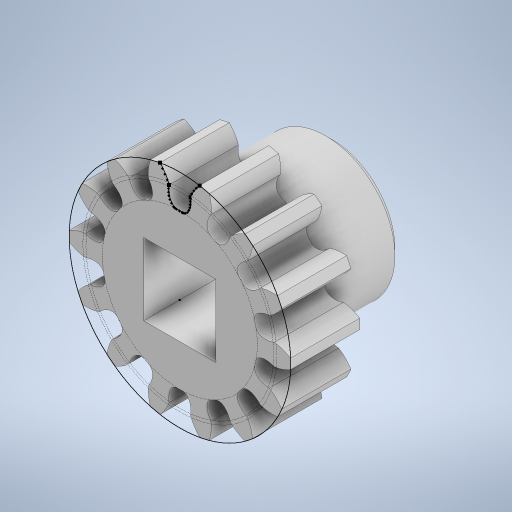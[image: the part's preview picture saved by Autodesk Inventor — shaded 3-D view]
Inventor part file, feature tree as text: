
AUTODESK INVENTOR PART (.ipt)
format: ipt  version: 2023 (Build 270158000, 158)  size: 937,984 bytes
history: native  units: in
note: dims shown in document units (in); Inventor stores cm internally (conversion verified against a paired STEP export)
features: sketch x5, extrude x5, pattern_circular x1, chamfer x1
ambient origin geometry x8: Origin, YZ Plane, XZ Plane, XY Plane, X Axis, Y Axis, Z Axis, Center Point
bodies: Solid1 (feature_tree)
feature tree (12):
  sketch  "Sketch1"  dims[d0=0.25in d1=0.0in]
  extrude  "Extrusion1"  TaperAngle=0.0deg  [1 undecoded]
  extrude  "Extrusion2"  Depth=5.5118in TaperAngle=360.0deg
  pattern_circular  "Circular Pattern1"  [2 undecoded]
  sketch  "Sketch2"  dims[d2=0.0in d3=0.0in d4=5.5118in d5=360.0deg]
  extrude  "Extrusion3"  Depth=0.1in TaperAngle=0.0deg
  extrude  "Extrusion5"  Depth=0.1in TaperAngle=45.0deg
  chamfer  "Chamfer2"  Distance=0.13in
  extrude  "Extrusion6"  Depth=0.13in
  sketch  "Sketch3"  dims[d7=0.26in]
  sketch  "Sketch5"  dims[d8=0.26in]
  sketch  "Sketch6"  dims[d9=0.15in d10=0.0in d15=0.5in d16=0.3in d17=0.0in d21=0.0236in d22=0.125in d23=45.0deg d24=0.13in d25=0.13in d26=0.1in d27=0.0in]
note: 3 required parameter values undecoded (feature->parameter linkage not recoverable at this tier; creation-order binding heuristic only, values carry confidence <= 0.55)
